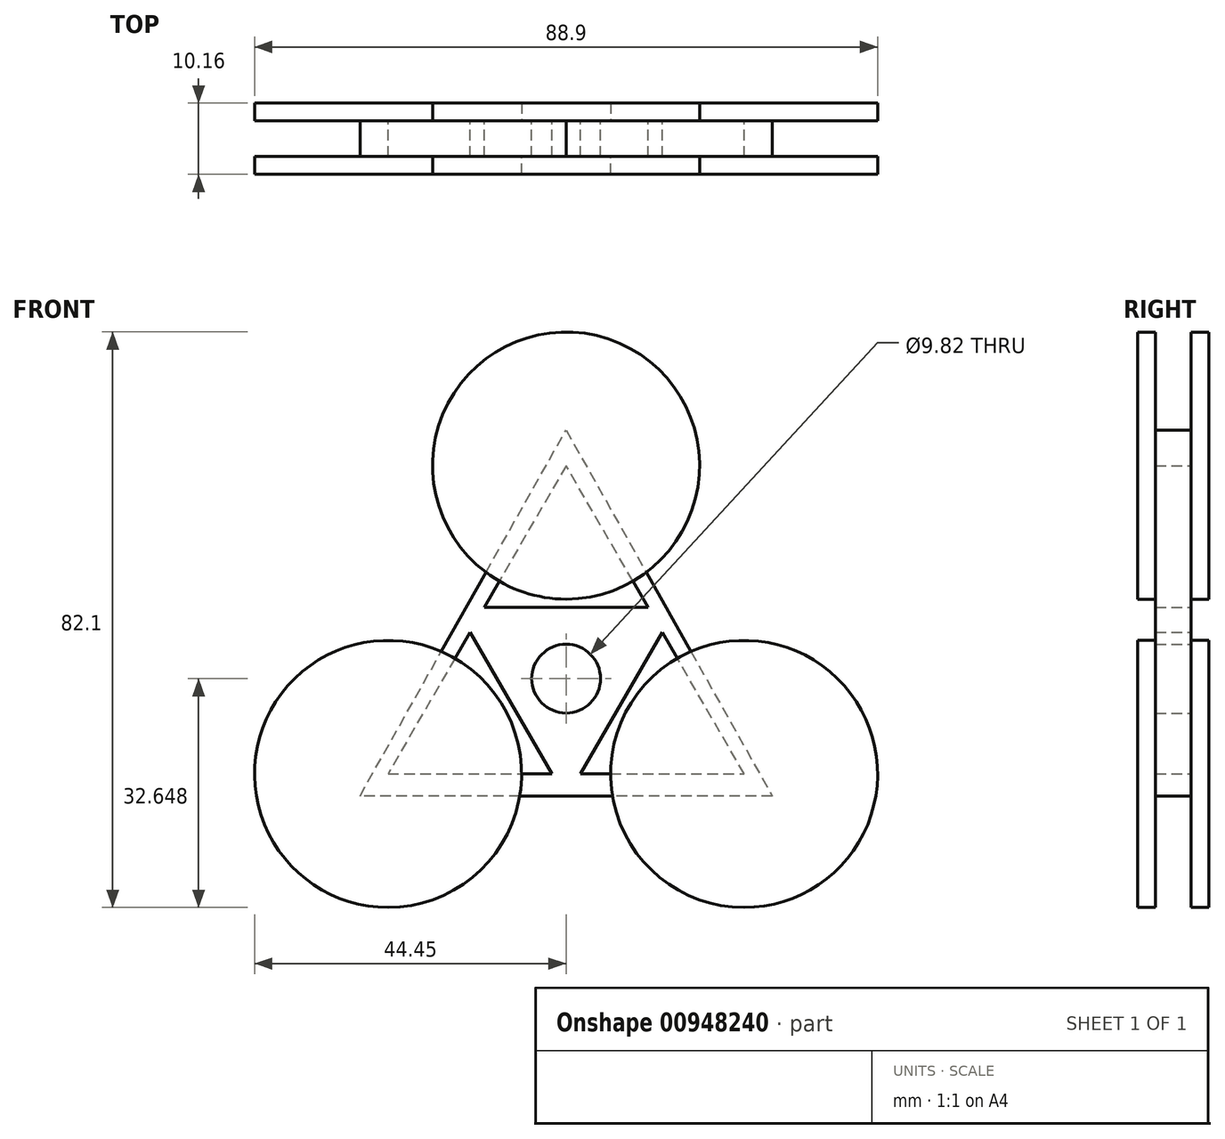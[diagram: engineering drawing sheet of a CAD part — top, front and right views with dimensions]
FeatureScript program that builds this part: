
annotation { "Feature Type Name" : "Feature", "Feature Type Description" : "" }
export const myFeature = defineFeature(function(context is Context, id is Id, definition is map)
    precondition{}
    {
        {
            var Q0;
            Q0=qCreatedBy(makeId("Front.planeOp"),FACE);
            var sketch = newSketch(context, id + "F0", { "sketchPlane" : qUnion([Q0])});
            skLineSegment(sketch, "E0", {"start": v(0, 11.67) * mm, "end": v(-25.4, -32.33) * mm});
            skLineSegment(sketch, "E1", {"start": v(-25.4, -32.33) * mm, "end": v(25.4, -32.33) * mm});
            skLineSegment(sketch, "E2", {"start": v(25.4, -32.33) * mm, "end": v(0, 11.67) * mm});
            skCircle(sketch, "E3", {"center": v(0, 11.67) * mm, "radius": 19.05 * mm});
            skCircle(sketch, "E4", {"center": v(25.4, -32.33) * mm, "radius": 19.05 * mm});
            skCircle(sketch, "E5", {"center": v(-25.4, -32.33) * mm, "radius": 19.05 * mm});
            skLineSegment(sketch, "E6", {"start": v(0, 11.67) * mm, "end": v(0, 16.75) * mm});
            skLineSegment(sketch, "E7", {"start": v(25.4, -32.33) * mm, "end": v(29.4, -35.45) * mm});
            skLineSegment(sketch, "E8", {"start": v(-25.4, -32.33) * mm, "end": v(-29.4, -35.45) * mm});
            skLineSegment(sketch, "E9", {"start": v(-29.4, -35.45) * mm, "end": v(0, 16.75) * mm});
            skLineSegment(sketch, "E10", {"start": v(0, 16.75) * mm, "end": v(29.4, -35.45) * mm});
            skLineSegment(sketch, "E11", {"start": v(29.4, -35.45) * mm, "end": v(-29.4, -35.45) * mm});
            skLineSegment(sketch, "E12", {"start": v(-12.7, -10.33) * mm, "end": v(-11.68, -8.57) * mm});
            skLineSegment(sketch, "E13", {"start": v(-12.7, -10.33) * mm, "end": v(-13.72, -12.1) * mm});
            skLineSegment(sketch, "E14", {"start": v(12.7, -10.33) * mm, "end": v(11.68, -8.57) * mm});
            skLineSegment(sketch, "E15", {"start": v(12.7, -10.33) * mm, "end": v(13.72, -12.1) * mm});
            skLineSegment(sketch, "E16", {"start": v(0, -32.33) * mm, "end": v(2.03, -32.33) * mm});
            skLineSegment(sketch, "E17", {"start": v(2.03, -32.33) * mm, "end": v(0, -32.33) * mm});
            skLineSegment(sketch, "E18", {"start": v(0, -32.33) * mm, "end": v(-2.03, -32.33) * mm});
            skLineSegment(sketch, "E19", {"start": v(-11.68, -8.57) * mm, "end": v(11.68, -8.57) * mm});
            skLineSegment(sketch, "E20", {"start": v(-13.72, -12.1) * mm, "end": v(-2.03, -32.33) * mm});
            skLineSegment(sketch, "E21", {"start": v(2.03, -32.33) * mm, "end": v(13.72, -12.1) * mm});
            skCircle(sketch, "E22", {"center": v(0, -18.73) * mm, "radius": 4.91 * mm});
            skSolve(sketch);
        }
        {
            var Q0;
            {var subQ0=sQuery(id+"F0.wireOp",EDGE,"E0");var subQ1=makeQuery(id+"F0.imprint","IMPRINT",VERTEX,{"derivedFrom":subQ0});Q0=makeQuery(id+"F0.imprint","IMPRINT",FACE,{"disambiguationData":[TD([[makeQuery(id+"F0.imprint","IMPRINT",EDGE,{"disambiguationData":[TD([[subQ1,-1.0]])],"derivedFrom":subQ0}),-1.0]])]});}
            var Q1;
            {var subQ0=sQuery(id+"F0.wireOp",EDGE,"E6");Q1=makeQuery(id+"F0.imprint","IMPRINT",FACE,{"disambiguationData":[TD([[makeQuery(id+"F0.imprint","IMPRINT",EDGE,{"derivedFrom":subQ0}),1.0]])]});}
            var Q2;
            {var subQ0=sQuery(id+"F0.wireOp",EDGE,"E8");Q2=makeQuery(id+"F0.imprint","IMPRINT",FACE,{"disambiguationData":[TD([[makeQuery(id+"F0.imprint","IMPRINT",EDGE,{"derivedFrom":subQ0}),-1.0]])]});}
            var Q3;
            {var subQ0=sQuery(id+"F0.wireOp",EDGE,"E8");Q3=makeQuery(id+"F0.imprint","IMPRINT",FACE,{"disambiguationData":[TD([[makeQuery(id+"F0.imprint","IMPRINT",EDGE,{"derivedFrom":subQ0}),1.0]])]});}
            var Q4;
            {var subQ0=sQuery(id+"F0.wireOp",EDGE,"E1");var subQ1=makeQuery(id+"F0.imprint","IMPRINT",VERTEX,{"derivedFrom":subQ0});Q4=makeQuery(id+"F0.imprint","IMPRINT",FACE,{"disambiguationData":[TD([[makeQuery(id+"F0.imprint","IMPRINT",EDGE,{"disambiguationData":[TD([[subQ1,-1.0]])],"derivedFrom":subQ0}),-1.0]])]});}
            var Q5;
            {var subQ3=sQuery(id+"F0.wireOp",EDGE,"E7");Q5=makeQuery(id+"F0.imprint","IMPRINT",FACE,{"disambiguationData":[TD([[makeQuery(id+"F0.imprint","IMPRINT",EDGE,{"derivedFrom":subQ3}),-1.0]])]});}
            var Q6;
            {var subQ0=sQuery(id+"F0.wireOp",EDGE,"E7");Q6=makeQuery(id+"F0.imprint","IMPRINT",FACE,{"disambiguationData":[TD([[makeQuery(id+"F0.imprint","IMPRINT",EDGE,{"derivedFrom":subQ0}),1.0]])]});}
            var Q7;
            {var subQ0=sQuery(id+"F0.wireOp",EDGE,"E2");var subQ1=makeQuery(id+"F0.imprint","IMPRINT",VERTEX,{"derivedFrom":subQ0});Q7=makeQuery(id+"F0.imprint","IMPRINT",FACE,{"disambiguationData":[TD([[makeQuery(id+"F0.imprint","IMPRINT",EDGE,{"disambiguationData":[TD([[subQ1,-1.0]])],"derivedFrom":subQ0}),-1.0]])]});}
            var Q8;
            {var subQ0=sQuery(id+"F0.wireOp",EDGE,"E6");Q8=makeQuery(id+"F0.imprint","IMPRINT",FACE,{"disambiguationData":[TD([[makeQuery(id+"F0.imprint","IMPRINT",EDGE,{"derivedFrom":subQ0}),-1.0]])]});}
            extrude(context, id + "F1", {"entities" : qUnion([Q0, Q1, Q2, Q3, Q4, Q5, Q6, Q7, Q8]), "depth" : 5.08 * mm, "offsetDistance" : 25.4 * mm});
        }
        {
            var Q0;
            {var subQ0=sQuery(id+"F0.wireOp",EDGE,"E9");var subQ1=sQuery(id+"F0.wireOp",EDGE,"E3");var subQ2=makeQuery(id+"F0.imprint","INTERSECT",VERTEX,{"derivedFrom":[subQ1,subQ0]});Q0=makeQuery(id+"F0.imprint","IMPRINT",FACE,{"disambiguationData":[TD([[makeQuery(id+"F0.imprint","IMPRINT",EDGE,{"disambiguationData":[TD([[subQ2,1.0]])],"derivedFrom":subQ1}),1.0]])]});}
            var Q1;
            {var subQ1=sQuery(id+"F0.wireOp",EDGE,"E0");var subQ3=sQuery(id+"F0.wireOp",EDGE,"E3");var subQ4=makeQuery(id+"F0.imprint","INTERSECT",VERTEX,{"derivedFrom":[subQ1,subQ3]});Q1=makeQuery(id+"F0.imprint","IMPRINT",FACE,{"disambiguationData":[TD([[makeQuery(id+"F0.imprint","IMPRINT",EDGE,{"disambiguationData":[TD([[subQ4,-1.0]])],"derivedFrom":subQ3}),1.0]])]});}
            var Q2;
            {var subQ0=sQuery(id+"F0.wireOp",EDGE,"E11");var subQ1=sQuery(id+"F0.wireOp",EDGE,"E5");var subQ2=makeQuery(id+"F0.imprint","INTERSECT",VERTEX,{"derivedFrom":[subQ1,subQ0]});Q2=makeQuery(id+"F0.imprint","IMPRINT",FACE,{"disambiguationData":[TD([[makeQuery(id+"F0.imprint","IMPRINT",EDGE,{"disambiguationData":[TD([[subQ2,1.0]])],"derivedFrom":subQ1}),1.0]])]});}
            var Q3;
            {var subQ1=sQuery(id+"F0.wireOp",EDGE,"E0");var subQ3=sQuery(id+"F0.wireOp",EDGE,"E5");var subQ4=makeQuery(id+"F0.imprint","INTERSECT",VERTEX,{"derivedFrom":[subQ1,subQ3]});Q3=makeQuery(id+"F0.imprint","IMPRINT",FACE,{"disambiguationData":[TD([[makeQuery(id+"F0.imprint","IMPRINT",EDGE,{"disambiguationData":[TD([[subQ4,1.0]])],"derivedFrom":subQ3}),1.0]])]});}
            var Q4;
            {var subQ0=sQuery(id+"F0.wireOp",EDGE,"E10");var subQ1=sQuery(id+"F0.wireOp",EDGE,"E4");var subQ2=makeQuery(id+"F0.imprint","INTERSECT",VERTEX,{"derivedFrom":[subQ1,subQ0]});Q4=makeQuery(id+"F0.imprint","IMPRINT",FACE,{"disambiguationData":[TD([[makeQuery(id+"F0.imprint","IMPRINT",EDGE,{"disambiguationData":[TD([[subQ2,1.0]])],"derivedFrom":subQ1}),1.0]])]});}
            var Q5;
            {var subQ0=sQuery(id+"F0.wireOp",EDGE,"E4");var subQ1=sQuery(id+"F0.wireOp",EDGE,"E1");var subQ2=makeQuery(id+"F0.imprint","INTERSECT",VERTEX,{"derivedFrom":[subQ1,subQ0]});Q5=makeQuery(id+"F0.imprint","IMPRINT",FACE,{"disambiguationData":[TD([[makeQuery(id+"F0.imprint","IMPRINT",EDGE,{"disambiguationData":[TD([[subQ2,1.0]])],"derivedFrom":subQ0}),1.0]])]});}
            var Q6;
            {var subQ0=sQuery(id+"F0.wireOp",EDGE,"E8");Q6=makeQuery(id+"F0.imprint","IMPRINT",FACE,{"disambiguationData":[TD([[makeQuery(id+"F0.imprint","IMPRINT",EDGE,{"derivedFrom":subQ0}),1.0]])]});}
            var Q7;
            {var subQ0=sQuery(id+"F0.wireOp",EDGE,"E8");Q7=makeQuery(id+"F0.imprint","IMPRINT",FACE,{"disambiguationData":[TD([[makeQuery(id+"F0.imprint","IMPRINT",EDGE,{"derivedFrom":subQ0}),-1.0]])]});}
            var Q8;
            {var subQ3=sQuery(id+"F0.wireOp",EDGE,"E7");Q8=makeQuery(id+"F0.imprint","IMPRINT",FACE,{"disambiguationData":[TD([[makeQuery(id+"F0.imprint","IMPRINT",EDGE,{"derivedFrom":subQ3}),-1.0]])]});}
            var Q9;
            {var subQ0=sQuery(id+"F0.wireOp",EDGE,"E7");Q9=makeQuery(id+"F0.imprint","IMPRINT",FACE,{"disambiguationData":[TD([[makeQuery(id+"F0.imprint","IMPRINT",EDGE,{"derivedFrom":subQ0}),1.0]])]});}
            var Q10;
            {var subQ0=sQuery(id+"F0.wireOp",EDGE,"E6");Q10=makeQuery(id+"F0.imprint","IMPRINT",FACE,{"disambiguationData":[TD([[makeQuery(id+"F0.imprint","IMPRINT",EDGE,{"derivedFrom":subQ0}),-1.0]])]});}
            var Q11;
            {var subQ0=sQuery(id+"F0.wireOp",EDGE,"E6");Q11=makeQuery(id+"F0.imprint","IMPRINT",FACE,{"disambiguationData":[TD([[makeQuery(id+"F0.imprint","IMPRINT",EDGE,{"derivedFrom":subQ0}),1.0]])]});}
            extrude(context, id + "F2", {"entities" : qUnion([Q0, Q1, Q2, Q3, Q4, Q5, Q6, Q7, Q8, Q9, Q10, Q11]), "operationType" : NewBodyOperationType.ADD, "oppositeDirection" : true, "depth" : 2.54 * mm, "offsetDistance" : 25.4 * mm});
        }
        {
            var Q0;
            Q0=makeQuery(id+"F1.opExtrude","CAP_FACE",FACE,{"disambiguationData":[OSD([sQuery(id+"F0.wireOp",EDGE,"E0"),sQuery(id+"F0.wireOp",EDGE,"E1"),sQuery(id+"F0.wireOp",EDGE,"E2"),sQuery(id+"F0.wireOp",EDGE,"E9"),sQuery(id+"F0.wireOp",EDGE,"E10"),sQuery(id+"F0.wireOp",EDGE,"E11")])],"isStart":false});
            var sketch = newSketch(context, id + "F3", { "sketchPlane" : qUnion([Q0])});
            skCircle(sketch, "E23", {"center": v(0, 11.67) * mm, "radius": 19.05 * mm});
            skCircle(sketch, "E24", {"center": v(25.4, -32.33) * mm, "radius": 19.05 * mm});
            skCircle(sketch, "E25", {"center": v(-25.4, -32.33) * mm, "radius": 19.05 * mm});
            skSolve(sketch);
        }
        {
            var Q0;
            {var subQ0=sQuery(id+"F3.wireOp",EDGE,"E23");var subQ1=makeQuery(id+"F1.opExtrude","CAP_EDGE",EDGE,{"disambiguationData":[OSD([sQuery(id+"F0.wireOp",EDGE,"E9")])],"isStart":false});var subQ2=makeQuery(id+"F3.imprint","INTERSECT",VERTEX,{"derivedFrom":[subQ1,subQ0]});Q0=makeQuery(id+"F3.imprint","IMPRINT",FACE,{"disambiguationData":[TD([[makeQuery(id+"F3.imprint","IMPRINT",EDGE,{"disambiguationData":[TD([[subQ2,1.0]])],"derivedFrom":subQ0}),1.0]])]});}
            var Q1;
            {var subQ0=sQuery(id+"F3.wireOp",EDGE,"E23");var subQ1=makeQuery(id+"F1.opExtrude","CAP_EDGE",EDGE,{"disambiguationData":[OSD([sQuery(id+"F0.wireOp",EDGE,"E0")])],"isStart":false});var subQ2=makeQuery(id+"F3.imprint","INTERSECT",VERTEX,{"derivedFrom":[subQ1,subQ0]});Q1=makeQuery(id+"F3.imprint","IMPRINT",FACE,{"disambiguationData":[TD([[makeQuery(id+"F3.imprint","IMPRINT",EDGE,{"disambiguationData":[TD([[subQ2,-1.0]])],"derivedFrom":subQ0}),1.0]])]});}
            var Q2;
            {var subQ3=sQuery(id+"F3.wireOp",EDGE,"E23");var subQ8=makeQuery(id+"F1.opExtrude","CAP_EDGE",EDGE,{"disambiguationData":[OSD([sQuery(id+"F0.wireOp",EDGE,"E9")])],"isStart":false});var subQ10=makeQuery(id+"F3.imprint","INTERSECT",VERTEX,{"derivedFrom":[subQ8,subQ3]});Q2=makeQuery(id+"F3.imprint","IMPRINT",FACE,{"disambiguationData":[TD([[makeQuery(id+"F3.imprint","IMPRINT",EDGE,{"disambiguationData":[TD([[subQ10,-1.0]])],"derivedFrom":subQ3}),1.0]])]});}
            var Q3;
            {var subQ0=sQuery(id+"F3.wireOp",EDGE,"E24");var subQ1=makeQuery(id+"F1.opExtrude","CAP_EDGE",EDGE,{"disambiguationData":[OSD([sQuery(id+"F0.wireOp",EDGE,"E10")])],"isStart":false});var subQ2=makeQuery(id+"F3.imprint","INTERSECT",VERTEX,{"derivedFrom":[subQ1,subQ0]});Q3=makeQuery(id+"F3.imprint","IMPRINT",FACE,{"disambiguationData":[TD([[makeQuery(id+"F3.imprint","IMPRINT",EDGE,{"disambiguationData":[TD([[subQ2,1.0]])],"derivedFrom":subQ0}),1.0]])]});}
            var Q4;
            {var subQ3=sQuery(id+"F3.wireOp",EDGE,"E24");var subQ5=makeQuery(id+"F1.opExtrude","CAP_EDGE",EDGE,{"disambiguationData":[OSD([sQuery(id+"F0.wireOp",EDGE,"E10")])],"isStart":false});var subQ6=makeQuery(id+"F3.imprint","INTERSECT",VERTEX,{"derivedFrom":[subQ5,subQ3]});Q4=makeQuery(id+"F3.imprint","IMPRINT",FACE,{"disambiguationData":[TD([[makeQuery(id+"F3.imprint","IMPRINT",EDGE,{"disambiguationData":[TD([[subQ6,-1.0]])],"derivedFrom":subQ3}),1.0]])]});}
            var Q5;
            {var subQ0=sQuery(id+"F3.wireOp",EDGE,"E24");var subQ1=makeQuery(id+"F1.opExtrude","CAP_EDGE",EDGE,{"disambiguationData":[OSD([sQuery(id+"F0.wireOp",EDGE,"E2")])],"isStart":false});var subQ2=makeQuery(id+"F3.imprint","INTERSECT",VERTEX,{"derivedFrom":[subQ1,subQ0]});Q5=makeQuery(id+"F3.imprint","IMPRINT",FACE,{"disambiguationData":[TD([[makeQuery(id+"F3.imprint","IMPRINT",EDGE,{"disambiguationData":[TD([[subQ2,-1.0]])],"derivedFrom":subQ0}),1.0]])]});}
            var Q6;
            {var subQ0=sQuery(id+"F3.wireOp",EDGE,"E25");var subQ1=makeQuery(id+"F1.opExtrude","CAP_EDGE",EDGE,{"disambiguationData":[OSD([sQuery(id+"F0.wireOp",EDGE,"E9")])],"isStart":false});var subQ2=makeQuery(id+"F3.imprint","INTERSECT",VERTEX,{"derivedFrom":[subQ1,subQ0]});Q6=makeQuery(id+"F3.imprint","IMPRINT",FACE,{"disambiguationData":[TD([[makeQuery(id+"F3.imprint","IMPRINT",EDGE,{"disambiguationData":[TD([[subQ2,-1.0]])],"derivedFrom":subQ0}),1.0]])]});}
            var Q7;
            {var subQ3=sQuery(id+"F3.wireOp",EDGE,"E25");var subQ8=makeQuery(id+"F1.opExtrude","CAP_EDGE",EDGE,{"disambiguationData":[OSD([sQuery(id+"F0.wireOp",EDGE,"E9")])],"isStart":false});var subQ10=makeQuery(id+"F3.imprint","INTERSECT",VERTEX,{"derivedFrom":[subQ8,subQ3]});Q7=makeQuery(id+"F3.imprint","IMPRINT",FACE,{"disambiguationData":[TD([[makeQuery(id+"F3.imprint","IMPRINT",EDGE,{"disambiguationData":[TD([[subQ10,1.0]])],"derivedFrom":subQ3}),1.0]])]});}
            var Q8;
            {var subQ0=sQuery(id+"F3.wireOp",EDGE,"E25");var subQ1=makeQuery(id+"F1.opExtrude","CAP_EDGE",EDGE,{"disambiguationData":[OSD([sQuery(id+"F0.wireOp",EDGE,"E0")])],"isStart":false});var subQ2=makeQuery(id+"F3.imprint","INTERSECT",VERTEX,{"derivedFrom":[subQ1,subQ0]});Q8=makeQuery(id+"F3.imprint","IMPRINT",FACE,{"disambiguationData":[TD([[makeQuery(id+"F3.imprint","IMPRINT",EDGE,{"disambiguationData":[TD([[subQ2,1.0]])],"derivedFrom":subQ0}),1.0]])]});}
            extrude(context, id + "F4", {"entities" : qUnion([Q0, Q1, Q2, Q3, Q4, Q5, Q6, Q7, Q8]), "operationType" : NewBodyOperationType.ADD, "depth" : 2.54 * mm, "offsetDistance" : 25.4 * mm});
        }
        {
            var Q0;
            {var subQ2=sQuery(id+"F0.wireOp",EDGE,"8uNmo8lO-Kncd-121p-vF3q-fV78YwRZtYda");Q0=makeQuery(id+"F0.imprint","IMPRINT",FACE,{"disambiguationData":[TD([[makeQuery(id+"F0.imprint","IMPRINT",EDGE,{"derivedFrom":subQ2}),1.0]])]});}
            var Q1;
            Q1=makeQuery(id+"F0.imprint","IMPRINT",FACE,{"disambiguationData":[TD([[makeQuery(id+"F0.imprint","IMPRINT",EDGE,{"derivedFrom":sQuery(id+"F0.wireOp",EDGE,"jRlR6pvZ-Fz8a-Tt7B-5TYd-JB6PJMv7QfKx")}),1.0]])]});
            var Q2;
            {var subQ6=sQuery(id+"F0.wireOp",EDGE,"E19");Q2=makeQuery(id+"F0.imprint","IMPRINT",FACE,{"disambiguationData":[TD([[makeQuery(id+"F0.imprint","IMPRINT",EDGE,{"derivedFrom":subQ6}),-1.0]])]});}
            extrude(context, id + "F5", {"entities" : qUnion([Q0, Q1, Q2]), "operationType" : NewBodyOperationType.ADD, "oppositeDirection" : true, "depth" : -5.08 * mm, "offsetDistance" : 25.4 * mm});
        }
    });
